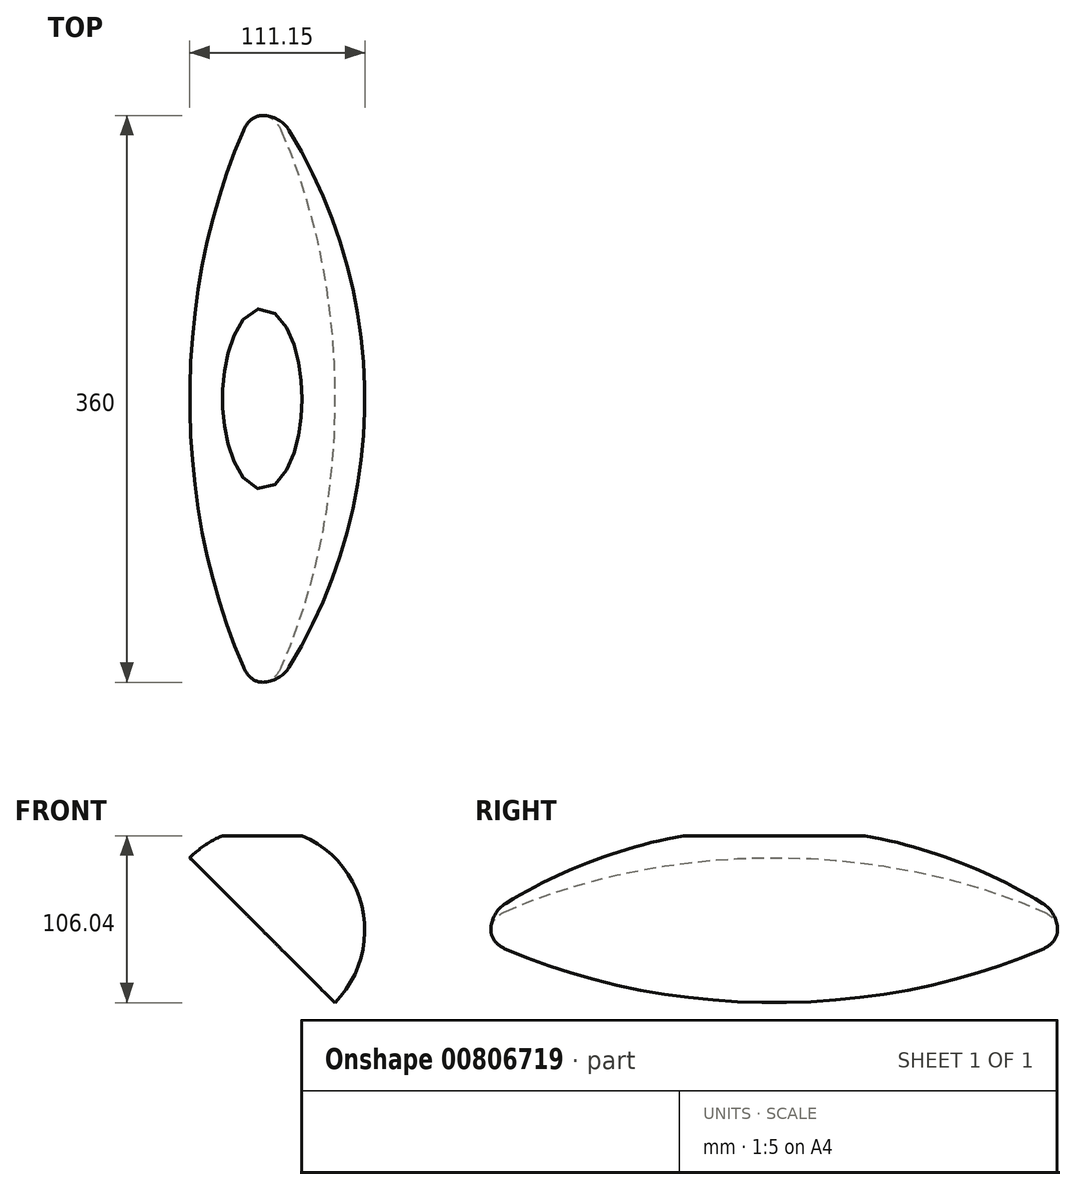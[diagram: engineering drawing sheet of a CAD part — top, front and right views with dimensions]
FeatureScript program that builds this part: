
annotation { "Feature Type Name" : "Feature", "Feature Type Description" : "" }
export const myFeature = defineFeature(function(context is Context, id is Id, definition is map)
    precondition{}
    {
        {
            var Q0;
            Q0=qCreatedBy(makeId("Right.planeOp"),FACE);
            var sketch = newSketch(context, id + "F0", { "sketchPlane" : qUnion([Q0])});
            skLineSegment(sketch, "E0", {"start": v(-180, 0) * mm, "end": v(180, 0) * mm});
            skArc(sketch, "E1", {"start": v(-170.45, 17.06) * mm, "mid": v(-177.45, 9.77) * mm, "end": v(-180, 0) * mm});
            skArc(sketch, "E2", {"start": v(180, 0) * mm, "mid": v(177.45, 9.77) * mm, "end": v(170.45, 17.06) * mm});
            skLineSegment(sketch, "E3", {"start": v(-180, 0) * mm, "end": v(-180, -15) * mm, "construction": true});
            skLineSegment(sketch, "E4", {"start": v(180, 0) * mm, "end": v(180, -15) * mm, "construction": true});
            skLineSegment(sketch, "E5", {"start": v(-57.5, 60) * mm, "end": v(57.5, 60) * mm, "construction": true});
            skLineSegment(sketch, "E6", {"start": v(0, 60) * mm, "end": v(0, 0) * mm, "construction": true});
            skArc(sketch, "E7", {"start": v(170.45, 17.06) * mm, "mid": v(0, 65.1) * mm, "end": v(-170.45, 17.06) * mm});
            skSolve(sketch);
        }
        {
            var Q0;
            Q0 = qSketchRegion(id + "F0", true);
            var Q1;
            Q1=sQuery(id+"F0.wireOp",EDGE,"E0");
            revolve(context, id + "F1", {"surfaceOperationType" : NewSurfaceOperationType.NEW, "entities" : qUnion([Q0]), "axis" : qUnion([Q1]), "revolveType" : RevolveType.FULL});
        }
        {
            var Q0;
            Q0=qCreatedBy(makeId("Right.planeOp"),FACE);
            var sketch = newSketch(context, id + "F2", { "sketchPlane" : qUnion([Q0])});
            skLineSegment(sketch, "E8.bottom", {"start": v(-75, -70) * mm, "end": v(75, -70) * mm});
            skLineSegment(sketch, "E8.top", {"start": v(-75, -60) * mm, "end": v(75, -60) * mm});
            skLineSegment(sketch, "E8.left", {"start": v(-75, -70) * mm, "end": v(-75, -60) * mm});
            skLineSegment(sketch, "E8.right", {"start": v(75, -70) * mm, "end": v(75, -60) * mm});
            skLineSegment(sketch, "E9.bottom", {"start": v(-75, 70) * mm, "end": v(75, 70) * mm});
            skLineSegment(sketch, "E9.top", {"start": v(-75, 60) * mm, "end": v(75, 60) * mm});
            skLineSegment(sketch, "E9.left", {"start": v(-75, 70) * mm, "end": v(-75, 60) * mm});
            skLineSegment(sketch, "E9.right", {"start": v(75, 70) * mm, "end": v(75, 60) * mm});
            skLineSegment(sketch, "E10", {"start": v(-170.45, 0) * mm, "end": v(170.45, 0) * mm});
            skLineSegment(sketch, "E11", {"start": v(0, 60) * mm, "end": v(0, 0) * mm});
            skSolve(sketch);
        }
        {
            var Q0;
            Q0 = qSketchRegion(id + "F2", true);
            extrude(context, id + "F3", {"entities" : qUnion([Q0]), "operationType" : NewBodyOperationType.REMOVE, "endBound" : BoundingType.SYMMETRIC, "depth" : 100 * mm, "offsetDistance" : 25 * mm});
        }
        {
            var Q0;
            Q0=qCreatedBy(makeId("Front.planeOp"),FACE);
            var sketch = newSketch(context, id + "F4", { "sketchPlane" : qUnion([Q0])});
            skLineSegment(sketch, "E12", {"start": v(-68.94, 68.94) * mm, "end": v(68.94, -68.94) * mm});
            skLineSegment(sketch, "E13", {"start": v(-68.94, 68.94) * mm, "end": v(-68.94, -68.94) * mm});
            skLineSegment(sketch, "E14", {"start": v(-68.94, -68.94) * mm, "end": v(68.94, -68.94) * mm});
            skSolve(sketch);
        }
        {
            var Q0;
            Q0 = qSketchRegion(id + "F4", true);
            extrude(context, id + "F5", {"entities" : qUnion([Q0]), "operationType" : NewBodyOperationType.REMOVE, "endBound" : BoundingType.SYMMETRIC, "oppositeDirection" : true, "depth" : 406 * mm, "offsetDistance" : 25 * mm});
        }
    });
